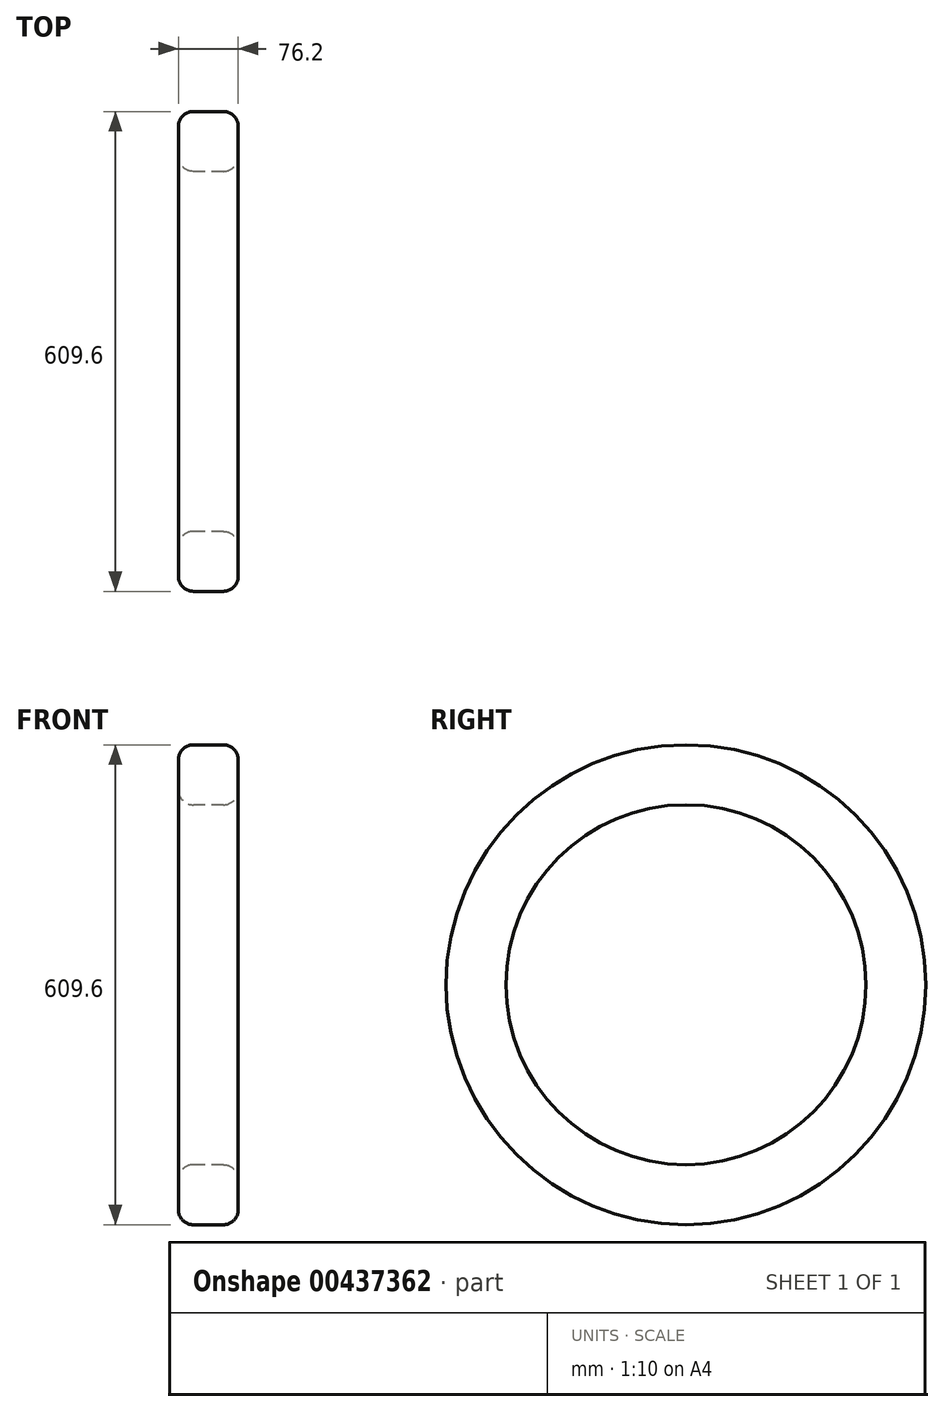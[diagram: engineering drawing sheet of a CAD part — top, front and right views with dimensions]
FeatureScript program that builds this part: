
annotation { "Feature Type Name" : "Feature", "Feature Type Description" : "" }
export const myFeature = defineFeature(function(context is Context, id is Id, definition is map)
    precondition{}
    {
        {
            var Q0;
            Q0=qCreatedBy(makeId("Top.planeOp"),FACE);
            var sketch = newSketch(context, id + "F0", { "sketchPlane" : qUnion([Q0])});
            skLineSegment(sketch, "E0", {"start": v(0, 0) * mm, "end": v(0, 228.6) * mm, "construction": true});
            skLineSegment(sketch, "E1.bottom", {"start": v(0, 228.6) * mm, "end": v(76.2, 228.6) * mm});
            skLineSegment(sketch, "E1.top", {"start": v(0, 304.8) * mm, "end": v(76.2, 304.8) * mm});
            skLineSegment(sketch, "E1.left", {"start": v(0, 228.6) * mm, "end": v(0, 304.8) * mm});
            skLineSegment(sketch, "E1.right", {"start": v(76.2, 228.6) * mm, "end": v(76.2, 304.8) * mm});
            skLineSegment(sketch, "E2", {"start": v(0, 0) * mm, "end": v(75.06, 0) * mm, "construction": true});
            skSolve(sketch);
        }
        {
            var Q0;
            Q0=makeQuery(id+"F0.imprint","IMPRINT",FACE,{"disambiguationData":[TD([[makeQuery(id+"F0.imprint","IMPRINT",EDGE,{"derivedFrom":sQuery(id+"F0.wireOp",EDGE,"E1.bottom")}),1.0]])]});
            var Q1;
            Q1=sQuery(id+"F0.wireOp",EDGE,"E2");
            revolve(context, id + "F1", {"entities" : qUnion([Q0]), "axis" : qUnion([Q1]), "revolveType" : RevolveType.FULL});
        }
        {
            var Q0;
            Q0=makeQuery(id+"F1.opRevolve","SWEPT_EDGE",EDGE,{"disambiguationData":[OSD([sQuery(id+"F0.wireOp",EDGE,"E1.bottom"),sQuery(id+"F0.wireOp",EDGE,"E1.right")])]});
            var Q1;
            Q1=makeQuery(id+"F1.opRevolve","SWEPT_EDGE",EDGE,{"disambiguationData":[OSD([sQuery(id+"F0.wireOp",EDGE,"E1.top"),sQuery(id+"F0.wireOp",EDGE,"E1.right")])]});
            var Q2;
            Q2=makeQuery(id+"F1.opRevolve","SWEPT_EDGE",EDGE,{"disambiguationData":[OSD([sQuery(id+"F0.wireOp",EDGE,"E1.top"),sQuery(id+"F0.wireOp",EDGE,"E1.left")])]});
            var Q3;
            Q3=makeQuery(id+"F1.opRevolve","SWEPT_EDGE",EDGE,{"disambiguationData":[OSD([sQuery(id+"F0.wireOp",EDGE,"E1.bottom"),sQuery(id+"F0.wireOp",EDGE,"E1.left")])]});
            fillet(context, id + "F2", {"entities" : qUnion([Q0, Q1, Q2, Q3]), "radius" : 19.05 * mm, "tangentPropagation" : true, "allowEdgeOverflow" : false});
        }
    });
